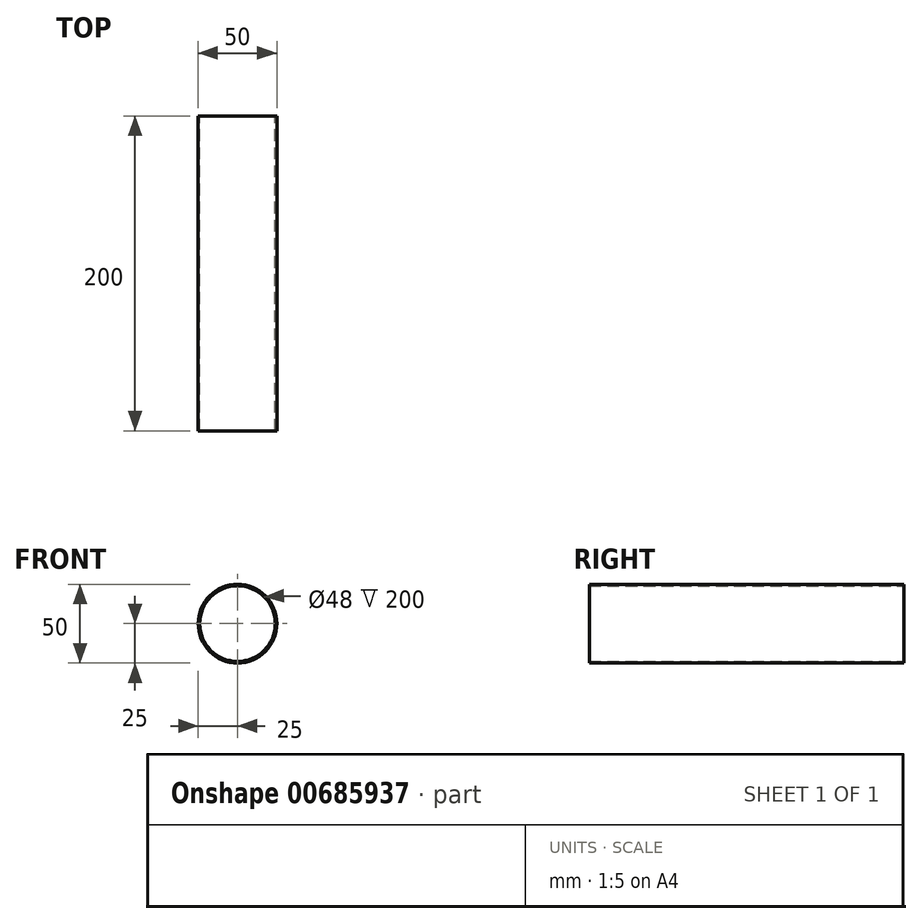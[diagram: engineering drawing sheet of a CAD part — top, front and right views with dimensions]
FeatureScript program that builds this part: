
annotation { "Feature Type Name" : "Feature", "Feature Type Description" : "" }
export const myFeature = defineFeature(function(context is Context, id is Id, definition is map)
    precondition{}
    {
        {
            var Q0;
            Q0=qCreatedBy(makeId("Front.planeOp"),FACE);
            var sketch = newSketch(context, id + "F0", { "sketchPlane" : qUnion([Q0])});
            skCircle(sketch, "E0", {"center": v(0, 0) * mm, "radius": 25 * mm});
            skSolve(sketch);
        }
        {
            var Q0;
            Q0=makeQuery(id+"F0.imprint","IMPRINT",FACE,{"disambiguationData":[TD([[makeQuery(id+"F0.imprint","IMPRINT",EDGE,{"derivedFrom":sQuery(id+"F0.wireOp",EDGE,"E0")}),1.0]])]});
            var Q1;
            Q1=sQuery(id+"F0.wireOp",EDGE,"E0");
            extrude(context, id + "F1", {"entities" : qUnion([Q0]), "surfaceEntities" : qUnion([Q1]), "depth" : 200 * mm, "offsetDistance" : 25 * mm});
        }
        {
            var Q0;
            Q0=makeQuery(id+"F1.opExtrude","CAP_FACE",FACE,{"disambiguationData":[OSD([sQuery(id+"F0.wireOp",EDGE,"E0")])],"isStart":false});
            var Q1;
            Q1=makeQuery(id+"F1.opExtrude","CAP_FACE",FACE,{"disambiguationData":[OSD([sQuery(id+"F0.wireOp",EDGE,"E0")])],"isStart":true});
            shell(context, id + "F2", {"entities" : qUnion([Q0, Q1]), "thickness" : 1 * mm});
        }
    });
